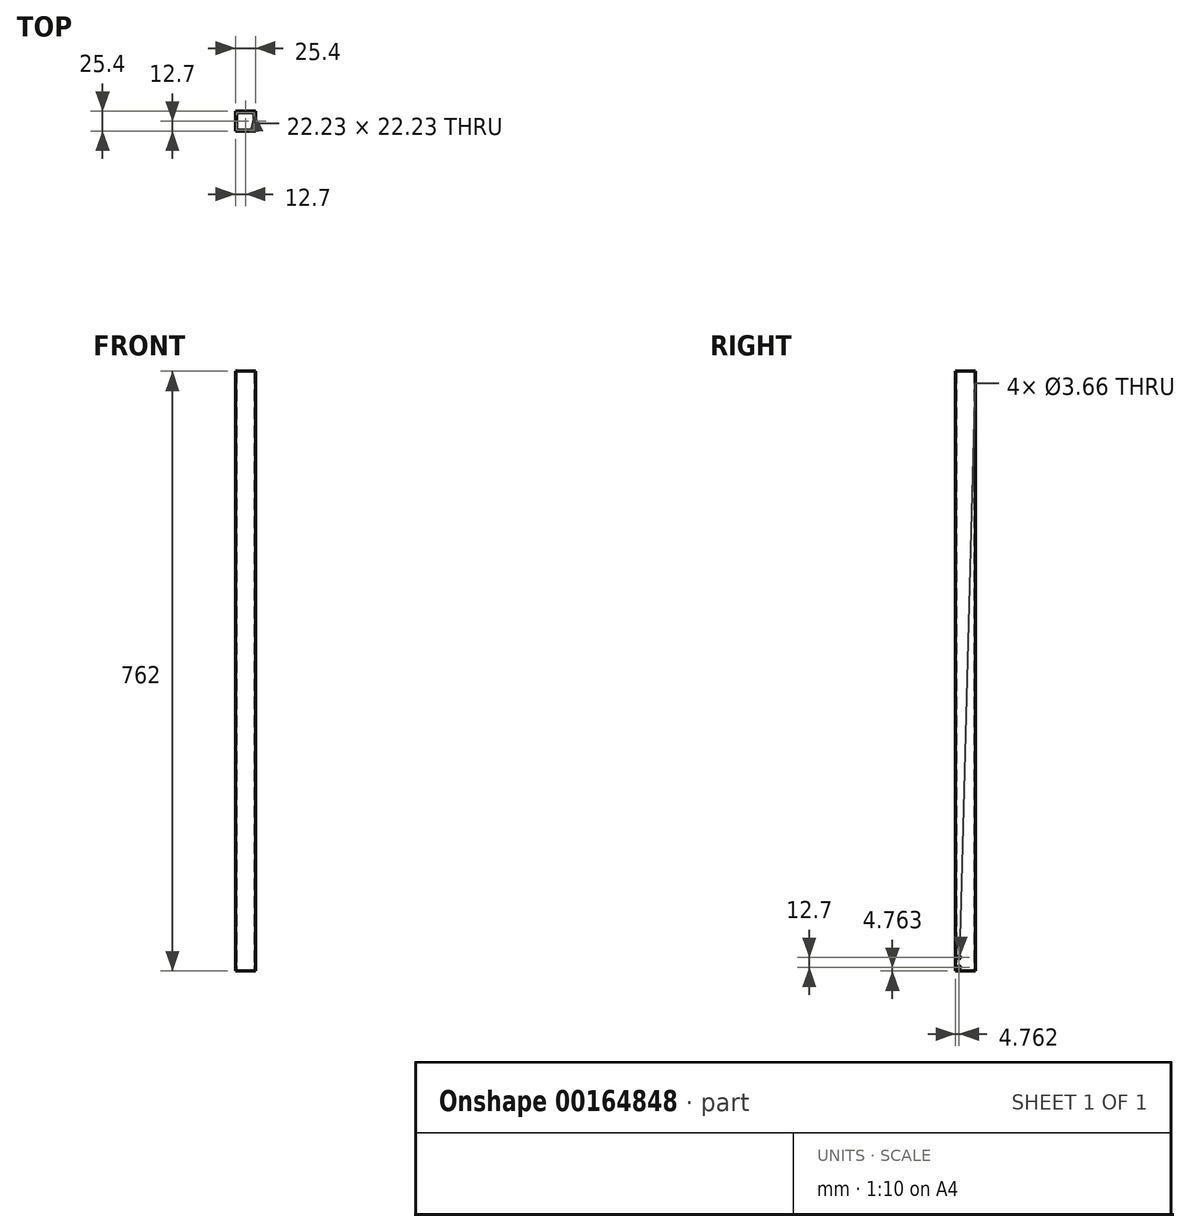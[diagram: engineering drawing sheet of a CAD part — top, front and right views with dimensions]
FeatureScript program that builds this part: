
annotation { "Feature Type Name" : "Feature", "Feature Type Description" : "" }
export const myFeature = defineFeature(function(context is Context, id is Id, definition is map)
    precondition{}
    {
        {
            var Q0;
            Q0=qCreatedBy(makeId("Top.planeOp"),FACE);
            var sketch = newSketch(context, id + "F0", { "sketchPlane" : qUnion([Q0])});
            skLineSegment(sketch, "E0.bottom", {"start": v(11.11, -11.11) * mm, "end": v(-11.11, -11.11) * mm});
            skLineSegment(sketch, "E0.top", {"start": v(11.11, 11.11) * mm, "end": v(-11.11, 11.11) * mm});
            skLineSegment(sketch, "E0.left", {"start": v(11.11, -11.11) * mm, "end": v(11.11, 11.11) * mm});
            skLineSegment(sketch, "E0.right", {"start": v(-11.11, -11.11) * mm, "end": v(-11.11, 11.11) * mm});
            skPoint(sketch, "E0.middle", {"position": v(0, 0) * mm});
            skLineSegment(sketch, "E1.bottom", {"start": v(12.7, -12.7) * mm, "end": v(-12.7, -12.7) * mm});
            skLineSegment(sketch, "E1.top", {"start": v(12.7, 12.7) * mm, "end": v(-12.7, 12.7) * mm});
            skLineSegment(sketch, "E1.left", {"start": v(12.7, -12.7) * mm, "end": v(12.7, 12.7) * mm});
            skLineSegment(sketch, "E1.right", {"start": v(-12.7, -12.7) * mm, "end": v(-12.7, 12.7) * mm});
            skSolve(sketch);
        }
        {
            var Q0;
            Q0=qSketchRegion(id+"F0",true);
            extrude(context, id + "F1", {"entities" : qUnion([Q0]), "depth" : 762 * mm});
        }
        {
            var Q0;
            Q0=makeQuery(id+"F1.opExtrude","SWEPT_FACE",FACE,{"disambiguationData":[OSD([sQuery(id+"F0.wireOp",EDGE,"E1.left")])]});
            var sketch = newSketch(context, id + "F2", { "sketchPlane" : qUnion([Q0])});
            skLineSegment(sketch, "E2", {"start": v(-7.94, 0) * mm, "end": v(-7.94, 4.76) * mm, "construction": true});
            skLineSegment(sketch, "E3", {"start": v(-7.94, 4.76) * mm, "end": v(-7.94, 17.46) * mm, "construction": true});
            skLineSegment(sketch, "E4", {"start": v(-7.94, 17.46) * mm, "end": v(-12.7, 17.46) * mm, "construction": true});
            skCircle(sketch, "E5", {"center": v(-7.94, 4.76) * mm, "radius": 1.83 * mm});
            skCircle(sketch, "E6", {"center": v(-7.94, 17.46) * mm, "radius": 1.83 * mm});
            skSolve(sketch);
        }
        {
            var Q0;
            Q0 = qSketchRegion(id + "F2", true);
            var Q1;
            Q1=makeQuery(id+"F1.opExtrude","SWEPT_FACE",FACE,{"disambiguationData":[OSD([sQuery(id+"F0.wireOp",EDGE,"E1.right")])]});
            extrude(context, id + "F3", {"entities" : qUnion([Q0]), "operationType" : NewBodyOperationType.REMOVE, "endBound" : BoundingType.UP_TO_SURFACE, "oppositeDirection" : true, "endBoundEntityFace" : qUnion([Q1]), "depth" : 25.4 * mm});
        }
    });
